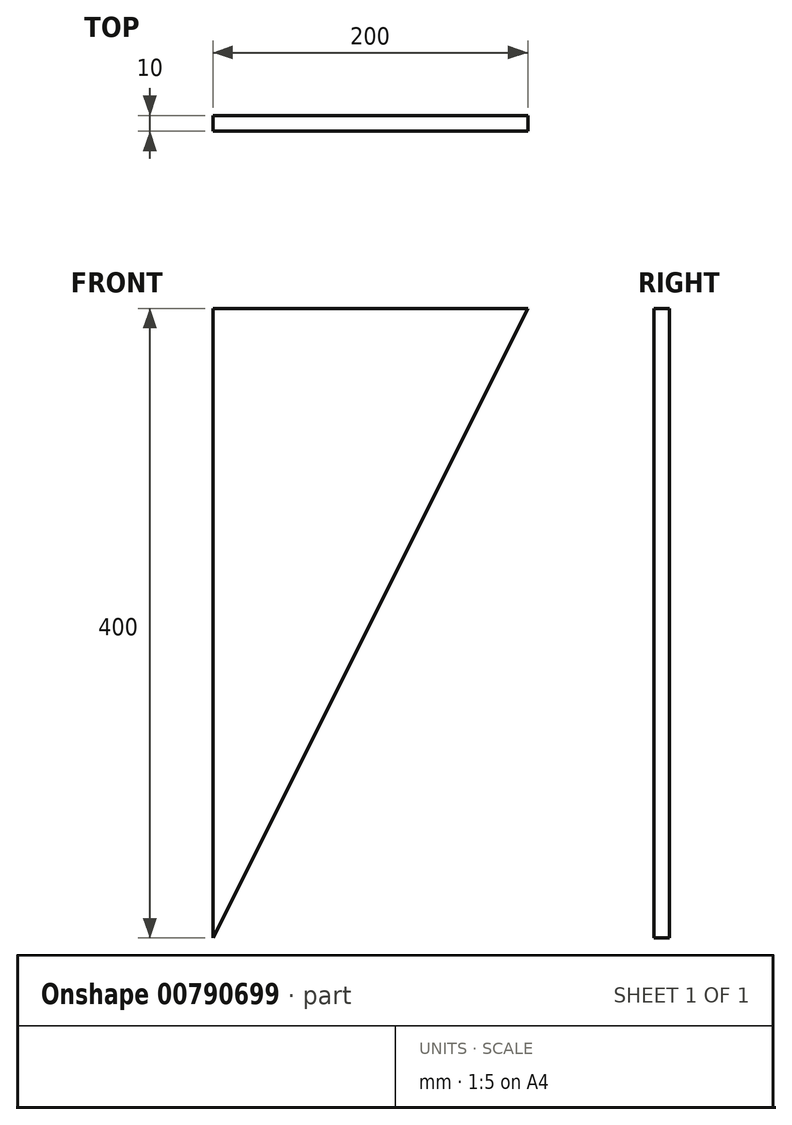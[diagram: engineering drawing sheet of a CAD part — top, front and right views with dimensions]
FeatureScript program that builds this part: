
annotation { "Feature Type Name" : "Feature", "Feature Type Description" : "" }
export const myFeature = defineFeature(function(context is Context, id is Id, definition is map)
    precondition{}
    {
        {
            var Q0;
            Q0=qCreatedBy(makeId("Front.planeOp"),FACE);
            var sketch = newSketch(context, id + "F0", { "sketchPlane" : qUnion([Q0])});
            skLineSegment(sketch, "E0", {"start": v(0, 0) * mm, "end": v(0, 400) * mm});
            skLineSegment(sketch, "E1", {"start": v(0, 400) * mm, "end": v(200, 400) * mm});
            skLineSegment(sketch, "E2", {"start": v(200, 400) * mm, "end": v(0, 0) * mm});
            skSolve(sketch);
        }
        {
            var Q0;
            Q0=makeQuery(id+"F0.imprint","IMPRINT",FACE,{"disambiguationData":[TD([[makeQuery(id+"F0.imprint","IMPRINT",EDGE,{"derivedFrom":sQuery(id+"F0.wireOp",EDGE,"E0")}),-1.0]])]});
            extrude(context, id + "F1", {"entities" : qUnion([Q0]), "depth" : 10 * mm, "offsetDistance" : 25 * mm});
        }
    });
